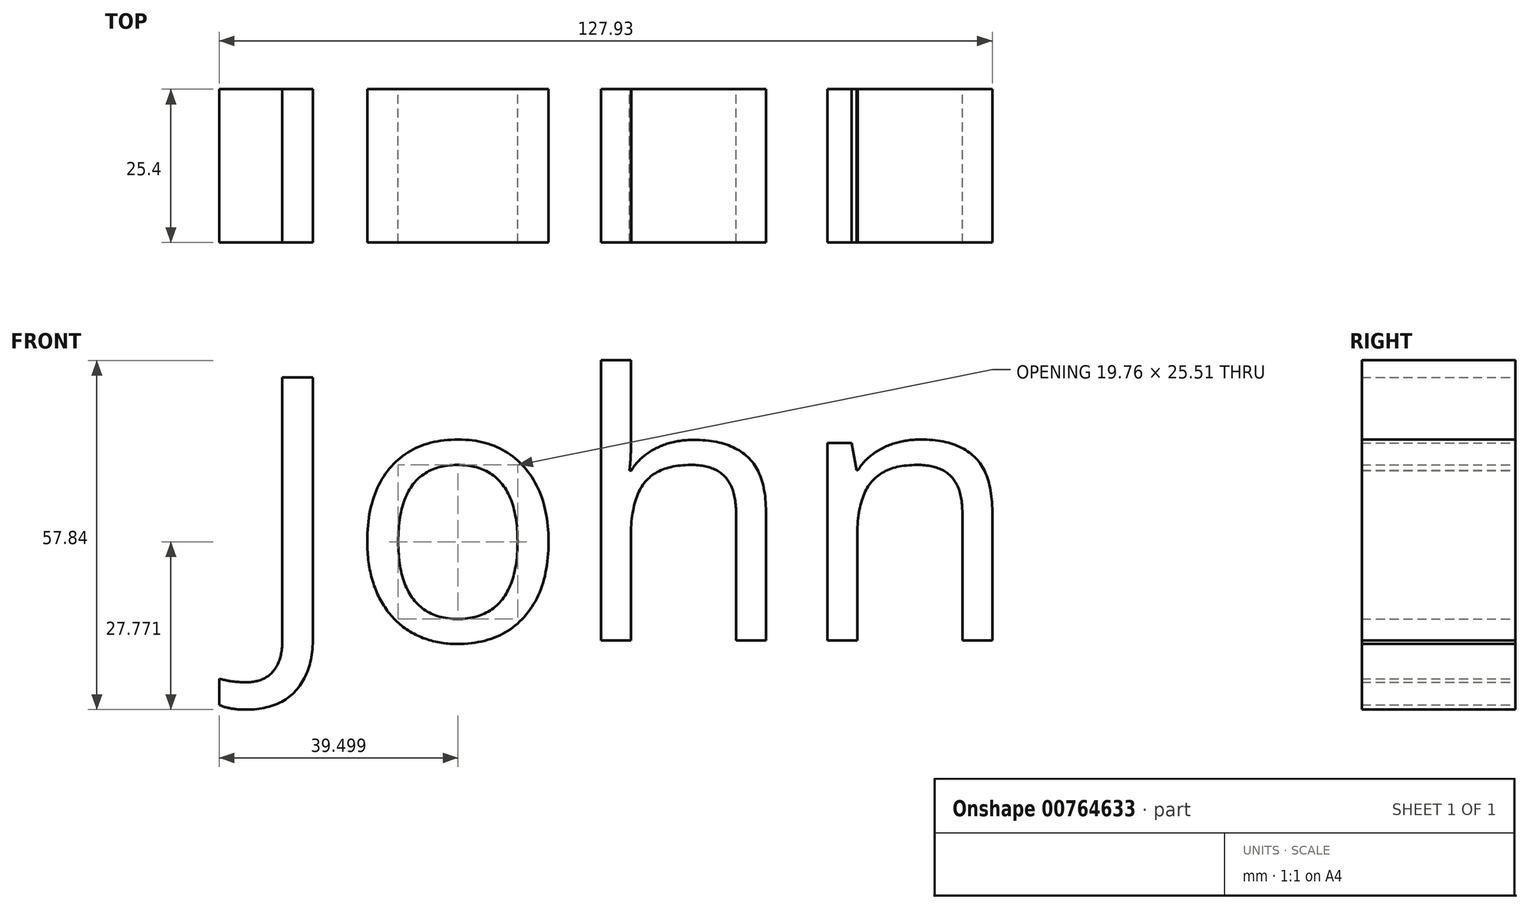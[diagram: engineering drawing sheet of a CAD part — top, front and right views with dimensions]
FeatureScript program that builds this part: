
annotation { "Feature Type Name" : "Feature", "Feature Type Description" : "" }
export const myFeature = defineFeature(function(context is Context, id is Id, definition is map)
    precondition{}
    {
        {
            var Q0;
            Q0=qCreatedBy(makeId("Front.planeOp"),FACE);
            var sketch = newSketch(context, id + "F0", { "sketchPlane" : qUnion([Q0])});
            skText(sketch, "E0", { "text": "John\n", "fontName": "OpenSans-Regular.ttf"});
            const initialGuessF0  = {"E0": [-0.03721, 0.02197, 1, 0, 0.04394]};
            skSetInitialGuess(sketch, initialGuessF0);
            skSolve(sketch);
        }
        {
            var Q0;
            Q0=makeQuery(id+"F0.imprint","IMPRINT",FACE,{"disambiguationData":[TD([[makeQuery(id+"F0.imprint","IMPRINT",EDGE,{"derivedFrom":sQuery(id+"F0.wireOp",EDGE,"E0.sketch_text.stroke-0")}),-1.0]])]});
            var Q1;
            Q1=makeQuery(id+"F0.imprint","IMPRINT",FACE,{"disambiguationData":[TD([[makeQuery(id+"F0.imprint","IMPRINT",EDGE,{"derivedFrom":sQuery(id+"F0.wireOp",EDGE,"E0.sketch_text.stroke-10")}),-1.0]])]});
            var Q2;
            Q2=makeQuery(id+"F0.imprint","IMPRINT",FACE,{"disambiguationData":[TD([[makeQuery(id+"F0.imprint","IMPRINT",EDGE,{"derivedFrom":sQuery(id+"F0.wireOp",EDGE,"E0.sketch_text.stroke-27")}),-1.0]])]});
            var Q3;
            Q3=makeQuery(id+"F0.imprint","IMPRINT",FACE,{"disambiguationData":[TD([[makeQuery(id+"F0.imprint","IMPRINT",EDGE,{"derivedFrom":sQuery(id+"F0.wireOp",EDGE,"E0.sketch_text.stroke-45")}),-1.0]])]});
            extrude(context, id + "F1", {"entities" : qUnion([Q0, Q1, Q2, Q3]), "depth" : 25.4 * mm, "offsetDistance" : 25.4 * mm});
        }
    });
